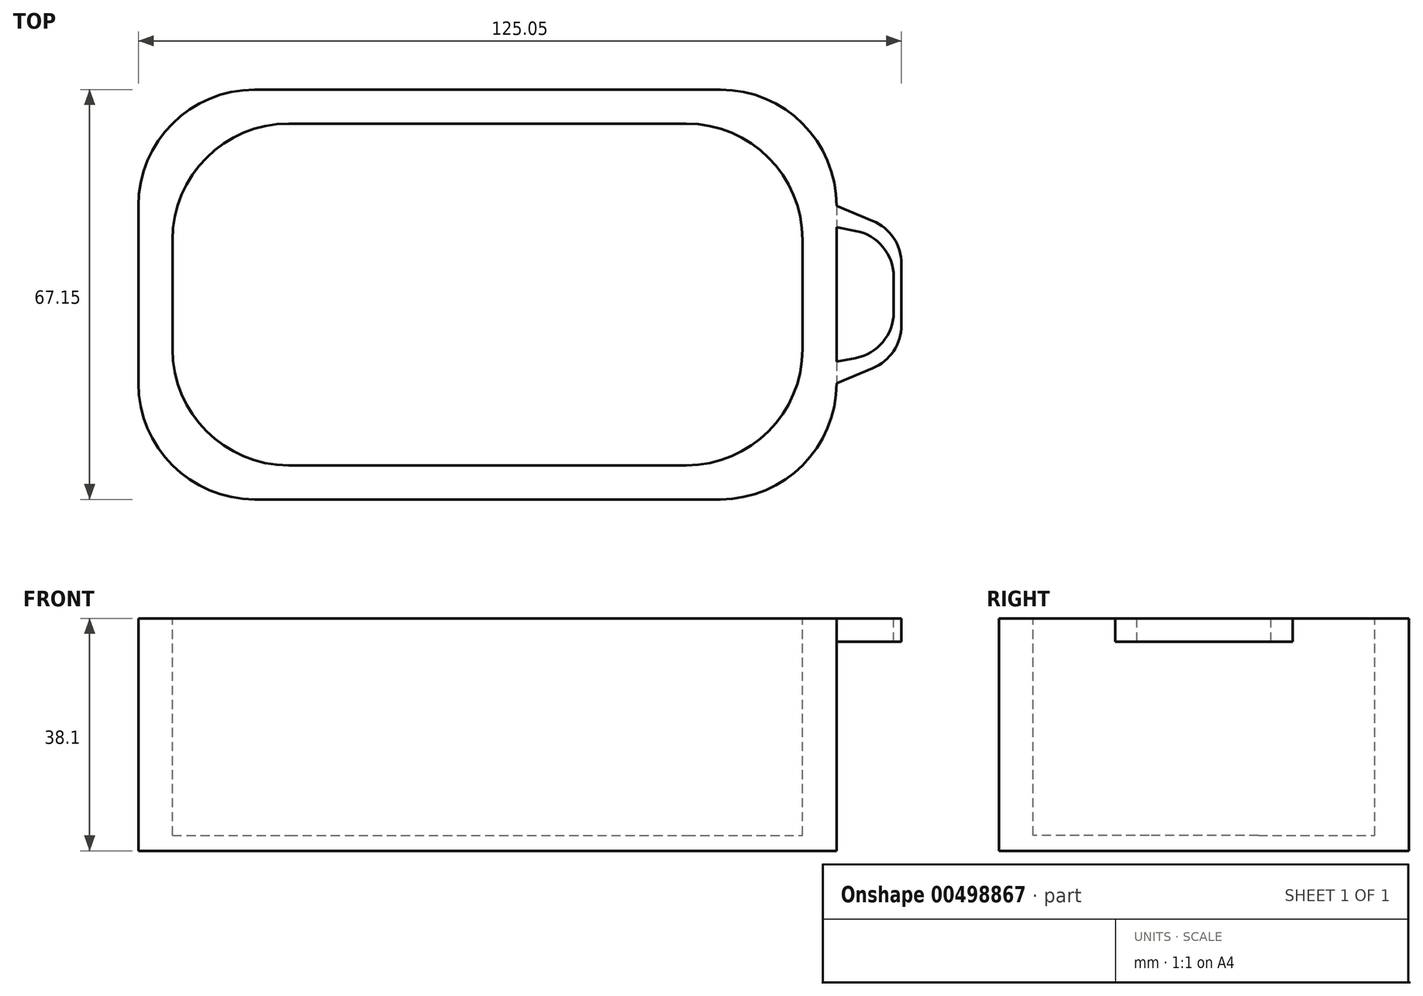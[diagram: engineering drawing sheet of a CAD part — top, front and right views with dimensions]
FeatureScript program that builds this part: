
annotation { "Feature Type Name" : "Feature", "Feature Type Description" : "" }
export const myFeature = defineFeature(function(context is Context, id is Id, definition is map)
    precondition{}
    {
        {
            var Q0;
            Q0=qCreatedBy(makeId("Top.planeOp"),FACE);
            var sketch = newSketch(context, id + "F0", { "sketchPlane" : qUnion([Q0])});
            skLineSegment(sketch, "E0.bottom", {"start": v(-47.42, 35.73) * mm, "end": v(28.9, 35.73) * mm});
            skLineSegment(sketch, "E0.top", {"start": v(-47.42, -31.42) * mm, "end": v(28.9, -31.42) * mm});
            skLineSegment(sketch, "E0.left", {"start": v(-66.47, 16.68) * mm, "end": v(-66.47, -12.37) * mm});
            skLineSegment(sketch, "E0.right", {"start": v(47.96, 16.68) * mm, "end": v(47.96, -12.37) * mm});
            skPoint(sketch, "E1.visualSharp", {"position": v(-66.47, 35.73) * mm});
            skArc(sketch, "E1.filletArc", {"start": v(-47.42, 35.73) * mm, "mid": v(-60.9, 30.15) * mm, "end": v(-66.47, 16.68) * mm});
            skPoint(sketch, "E2.visualSharp", {"position": v(-66.47, -31.42) * mm});
            skArc(sketch, "E2.filletArc", {"start": v(-66.47, -12.37) * mm, "mid": v(-60.9, -25.84) * mm, "end": v(-47.42, -31.42) * mm});
            skPoint(sketch, "E3.visualSharp", {"position": v(47.96, -31.42) * mm});
            skArc(sketch, "E3.filletArc", {"start": v(28.9, -31.42) * mm, "mid": v(42.38, -25.84) * mm, "end": v(47.96, -12.37) * mm});
            skPoint(sketch, "E4.visualSharp", {"position": v(47.96, 35.73) * mm});
            skArc(sketch, "E4.filletArc", {"start": v(47.96, 16.68) * mm, "mid": v(42.38, 30.15) * mm, "end": v(28.9, 35.73) * mm});
            skSolve(sketch);
        }
        {
            var Q0;
            Q0=makeQuery(id+"F0.imprint","IMPRINT",FACE,{"disambiguationData":[TD([[makeQuery(id+"F0.imprint","IMPRINT",EDGE,{"derivedFrom":sQuery(id+"F0.wireOp",EDGE,"E0.bottom")}),-1.0]])]});
            extrude(context, id + "F1", {"entities" : qUnion([Q0]), "depth" : 38.1 * mm, "offsetDistance" : 25.4 * mm});
        }
        {
            var Q0;
            Q0=makeQuery(id+"F1.opExtrude","CAP_FACE",FACE,{"disambiguationData":[OSD([sQuery(id+"F0.wireOp",EDGE,"E0.bottom"),sQuery(id+"F0.wireOp",EDGE,"E0.top"),sQuery(id+"F0.wireOp",EDGE,"E0.left"),sQuery(id+"F0.wireOp",EDGE,"E0.right"),sQuery(id+"F0.wireOp",EDGE,"E1.filletArc"),sQuery(id+"F0.wireOp",EDGE,"E2.filletArc"),sQuery(id+"F0.wireOp",EDGE,"E3.filletArc"),sQuery(id+"F0.wireOp",EDGE,"E4.filletArc")])],"isStart":false});
            var sketch = newSketch(context, id + "F2", { "sketchPlane" : qUnion([Q0])});
            skLineSegment(sketch, "E5.bottom", {"start": v(-41.85, 30.15) * mm, "end": v(23.33, 30.15) * mm});
            skLineSegment(sketch, "E5.top", {"start": v(-41.85, -25.84) * mm, "end": v(23.33, -25.84) * mm});
            skLineSegment(sketch, "E5.left", {"start": v(-60.9, 11.1) * mm, "end": v(-60.9, -6.79) * mm});
            skLineSegment(sketch, "E5.right", {"start": v(42.38, 11.1) * mm, "end": v(42.38, -6.79) * mm});
            skPoint(sketch, "E6.visualSharp", {"position": v(-60.9, 30.15) * mm});
            skArc(sketch, "E6.filletArc", {"start": v(-41.85, 30.15) * mm, "mid": v(-55.32, 24.57) * mm, "end": v(-60.9, 11.1) * mm});
            skPoint(sketch, "E7.visualSharp", {"position": v(-60.9, -25.84) * mm});
            skArc(sketch, "E7.filletArc", {"start": v(-60.9, -6.79) * mm, "mid": v(-55.32, -20.26) * mm, "end": v(-41.85, -25.84) * mm});
            skPoint(sketch, "E8.visualSharp", {"position": v(42.38, -25.84) * mm});
            skArc(sketch, "E8.filletArc", {"start": v(23.33, -25.84) * mm, "mid": v(36.8, -20.26) * mm, "end": v(42.38, -6.79) * mm});
            skPoint(sketch, "E9.visualSharp", {"position": v(42.38, 30.15) * mm});
            skArc(sketch, "E9.filletArc", {"start": v(42.38, 11.1) * mm, "mid": v(36.8, 24.57) * mm, "end": v(23.33, 30.15) * mm});
            skSolve(sketch);
        }
        {
            var Q0;
            Q0=makeQuery(id+"F2.imprint","IMPRINT",FACE,{"disambiguationData":[TD([[makeQuery(id+"F2.imprint","IMPRINT",EDGE,{"derivedFrom":sQuery(id+"F2.wireOp",EDGE,"E5.bottom")}),-1.0]])]});
            extrude(context, id + "F3", {"entities" : qUnion([Q0]), "operationType" : NewBodyOperationType.REMOVE, "oppositeDirection" : true, "depth" : 35.56 * mm, "offsetDistance" : 25.4 * mm});
        }
        {
            var Q0;
            Q0=makeQuery(id+"F1.opExtrude","CAP_FACE",FACE,{"disambiguationData":[OSD([sQuery(id+"F0.wireOp",EDGE,"E0.bottom"),sQuery(id+"F0.wireOp",EDGE,"E0.top"),sQuery(id+"F0.wireOp",EDGE,"E0.left"),sQuery(id+"F0.wireOp",EDGE,"E0.right"),sQuery(id+"F0.wireOp",EDGE,"E1.filletArc"),sQuery(id+"F0.wireOp",EDGE,"E2.filletArc"),sQuery(id+"F0.wireOp",EDGE,"E3.filletArc"),sQuery(id+"F0.wireOp",EDGE,"E4.filletArc")])],"isStart":false});
            var sketch = newSketch(context, id + "F4", { "sketchPlane" : qUnion([Q0])});
            skLineSegment(sketch, "E10", {"start": v(47.96, -12.37) * mm, "end": v(53.88, -9.91) * mm});
            skPoint(sketch, "E11.endSnap0", {"position": v(47.96, 2.16) * mm});
            skLineSegment(sketch, "E12.MirrorCS", {"start": v(47.96, 16.68) * mm, "end": v(53.88, 14.22) * mm});
            skLineSegment(sketch, "E13", {"start": v(58.58, -2.87) * mm, "end": v(58.58, 7.19) * mm});
            skPoint(sketch, "E14.visualSharp", {"position": v(58.58, -7.96) * mm});
            skArc(sketch, "E14.filletArc", {"start": v(53.88, -9.91) * mm, "mid": v(57.3, -7.1) * mm, "end": v(58.58, -2.87) * mm});
            skPoint(sketch, "E15.visualSharp", {"position": v(58.58, 12.27) * mm});
            skArc(sketch, "E15.filletArc", {"start": v(58.58, 7.19) * mm, "mid": v(57.3, 11.42) * mm, "end": v(53.88, 14.22) * mm});
            skLineSegment(sketch, "E16", {"start": v(47.96, -8.85) * mm, "end": v(51.08, -8.27) * mm});
            skLineSegment(sketch, "E17.MirrorCS", {"start": v(47.96, 13.16) * mm, "end": v(51.08, 12.58) * mm});
            skLineSegment(sketch, "E18", {"start": v(57.3, -0.78) * mm, "end": v(57.3, 5.09) * mm});
            skPoint(sketch, "E19.visualSharp", {"position": v(57.3, -7.1) * mm});
            skArc(sketch, "E19.filletArc", {"start": v(51.08, -8.27) * mm, "mid": v(55.54, -5.65) * mm, "end": v(57.3, -0.78) * mm});
            skPoint(sketch, "E20.visualSharp", {"position": v(57.3, 11.42) * mm});
            skArc(sketch, "E20.filletArc", {"start": v(57.3, 5.09) * mm, "mid": v(55.54, 9.96) * mm, "end": v(51.08, 12.58) * mm});
            skArc(sketch, "E21.MirrorCS", {"start": v(-77.1, 7.19) * mm, "mid": v(-75.81, 11.42) * mm, "end": v(-72.4, 14.22) * mm});
            skLineSegment(sketch, "E22.MirrorCS", {"start": v(-66.47, 13.16) * mm, "end": v(-69.6, 12.58) * mm});
            skLineSegment(sketch, "E23.MirrorCS", {"start": v(-66.47, -8.85) * mm, "end": v(-69.6, -8.27) * mm});
            skArc(sketch, "E24.MirrorCS", {"start": v(-72.4, -9.91) * mm, "mid": v(-75.81, -7.1) * mm, "end": v(-77.1, -2.87) * mm});
            skPoint(sketch, "E25.MirrorP", {"position": v(-75.81, 11.42) * mm});
            skPoint(sketch, "E26.MirrorP", {"position": v(-66.47, 2.16) * mm});
            skLineSegment(sketch, "E27.MirrorCS", {"start": v(-75.81, -0.78) * mm, "end": v(-75.81, 5.09) * mm});
            skArc(sketch, "E28.MirrorCS", {"start": v(-69.6, -8.27) * mm, "mid": v(-74.06, -5.65) * mm, "end": v(-75.81, -0.78) * mm});
            skPoint(sketch, "E29.MirrorP", {"position": v(-75.81, -7.1) * mm});
            skPoint(sketch, "E30.MirrorP", {"position": v(-77.1, -7.96) * mm});
            skPoint(sketch, "E31.MirrorP", {"position": v(-77.1, 12.27) * mm});
            skLineSegment(sketch, "E32.MirrorCS", {"start": v(-77.1, -2.87) * mm, "end": v(-77.1, 7.19) * mm});
            skArc(sketch, "E33.MirrorCS", {"start": v(-75.81, 5.09) * mm, "mid": v(-74.06, 9.96) * mm, "end": v(-69.6, 12.58) * mm});
            skLineSegment(sketch, "E34.MirrorCS", {"start": v(-66.47, 16.68) * mm, "end": v(-72.4, 14.22) * mm});
            skLineSegment(sketch, "E35.MirrorCS", {"start": v(-66.47, -12.37) * mm, "end": v(-72.4, -9.91) * mm});
            skSolve(sketch);
        }
        {
            var Q0;
            {var subQ2=sQuery(id+"F4.wireOp",EDGE,"E10");Q0=makeQuery(id+"F4.imprint","IMPRINT",FACE,{"disambiguationData":[TD([[makeQuery(id+"F4.imprint","IMPRINT",EDGE,{"derivedFrom":subQ2}),1.0]])]});}
            var Q1;
            Q1=makeQuery(id+"F4.imprint","IMPRINT",FACE,{"disambiguationData":[TD([[makeQuery(id+"F4.imprint","IMPRINT",EDGE,{"derivedFrom":sQuery(id+"F4.wireOp",EDGE,"E21.MirrorCS")}),-1.0]])]});
            extrude(context, id + "F5", {"entities" : qUnion([Q0, Q1]), "operationType" : NewBodyOperationType.ADD, "oppositeDirection" : true, "depth" : 3.8 * mm, "offsetDistance" : 25.4 * mm});
        }
    });
